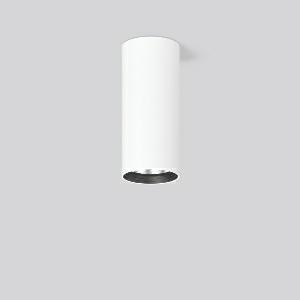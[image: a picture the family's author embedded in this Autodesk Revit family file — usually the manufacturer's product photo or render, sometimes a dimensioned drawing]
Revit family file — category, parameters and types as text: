
# Revit family: heledon_mini_a_931209_002_2_4473
name_source: partatom
category: Lighting Fixtures
units: mm (PartAtom-declared; Revit-internal decimal feet)

## family parameters
Cut with Voids When Loaded = No
Host = Face
Light Source = No
Part Type = Normal
Room Calculation Point = No
Round Connector Dimension = Use Diameter
Shared = No

## types (1)
- HELEDON mini A (1 x LED Modul 927, 3300 lm, 2700)
    Apparent Load = 29 VA
    Approval mark = CE
    CIE Flux Codes = 99 100 100 100 100
    Color Rendering = 92
    Color Temperature = 2700
    Default Elevation = 1800 mm
    Description = Series: HELEDON mini
Cylindrical surface-mounted downlight. Housing: die-cast aluminium, powder-coated. Internal ceiling frame polycarbonate with bayonet mounting. Black plastic ring and recessed LED to prevent glare from the side. Optical assembly with reflector made of MIRO-Silver with 98% total light reflection for outstanding efficiency - can be changed without tools. Best colour rendering index Ra>90. Suitable for Ceiling mounting. Easy installation with a separate ceiling frame with bayonet mounting and plug connection. Driver integrated. Connected via plug-in connector. High quality converter without flickering and stroboscopic effect. The following accessories can be mounted without use of tools: interchangeable lenses, decorative glasses, honeycomb louvre, clear and frosted diffusers, white interchangeable plastic ring. 
Colour: traffic white, matt (RAL 9016)
Diameter: 87 mm
Height: 197 mm
Lamp: LED
Socket: without socket
Colour temperature: 2700K
Colour rendering index (CRI): 92
System power: 29 W
Rated luminous flux: 3300 lm
Luminous efficiency: 114 lm/W
Control gear: Regulated power supply
Protection class: I
Type of protection: IP 20
    Height = 197 mm
    Lamp = 1 x LED Modul 927
    Lamp Light Flux = 3300 lm
    Lamp count = 1
    Length = 87 mm
    Lifetime = 50000 h
    Luminous efficacy = 114 lm/W
    Manufacturer = RZB
    ModVariant = No
    Model = 931209.002.2
    Mounting Place = Ceiling
    Mounting Type = Surface mounted
    Number of Poles = 1
    OnlyDefault = Yes
    Power Factor = 1
    Product Name = HELEDON mini A
    Product group = Surface mounted downlights
    ProductGroupID = 302
    Protection Class = Protection class I
    Protection Degree = IP 20
    RLX_Detail_Level = 1
    RLX_Emergency_Light_Flux = 0 lm
    RLX_Emergency_Type = 0
    RLX_Emergency_Type_DB = No
    RlxData = <blob elided: 107345 chars, md5=37808924>
    Socket = socket
    Standby Power = 0 W
    System Light Flux = 3300 lm
    System Power = 29 W
    Type Comments = Product without accessories
    Type Image = 931188.002.jpg
    URL = http://relux.com
    VarID = ---
    Voltage = 230 V
    Voltage Range = 220-240 V
    Weight = 0.00 kg
    Width = 0 mm  [stored 0 ft]

note: [stored X ft] marks values corroborated as IEEE doubles in the binary element streams (Revit-internal decimal feet)

## geometry (parser evidence)
native form markers: Blend x4, Sweep x10
no freeform markers — native parametric forms only
